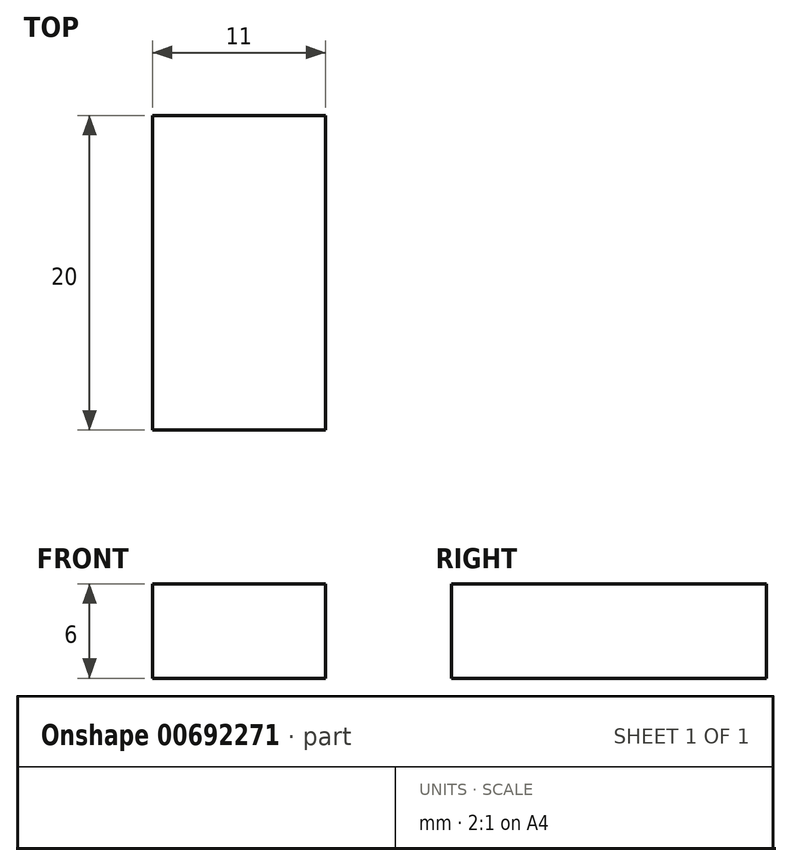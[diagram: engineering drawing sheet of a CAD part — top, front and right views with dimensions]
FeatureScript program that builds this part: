
annotation { "Feature Type Name" : "Feature", "Feature Type Description" : "" }
export const myFeature = defineFeature(function(context is Context, id is Id, definition is map)
    precondition{}
    {
        {
            var Q0;
            Q0=qCreatedBy(makeId("Top.planeOp"),FACE);
            var sketch = newSketch(context, id + "F0", { "sketchPlane" : qUnion([Q0])});
            skLineSegment(sketch, "E0.bottom", {"start": v(0, 0) * mm, "end": v(11, 0) * mm});
            skLineSegment(sketch, "E0.top", {"start": v(0, 20) * mm, "end": v(11, 20) * mm});
            skLineSegment(sketch, "E0.left", {"start": v(0, 0) * mm, "end": v(0, 20) * mm});
            skLineSegment(sketch, "E0.right", {"start": v(11, 0) * mm, "end": v(11, 20) * mm});
            skSolve(sketch);
        }
        {
            var Q0;
            Q0 = qSketchRegion(id + "F0", true);
            extrude(context, id + "F1", {"entities" : qUnion([Q0]), "depth" : 6 * mm, "offsetDistance" : 25.4 * mm});
        }
    });
